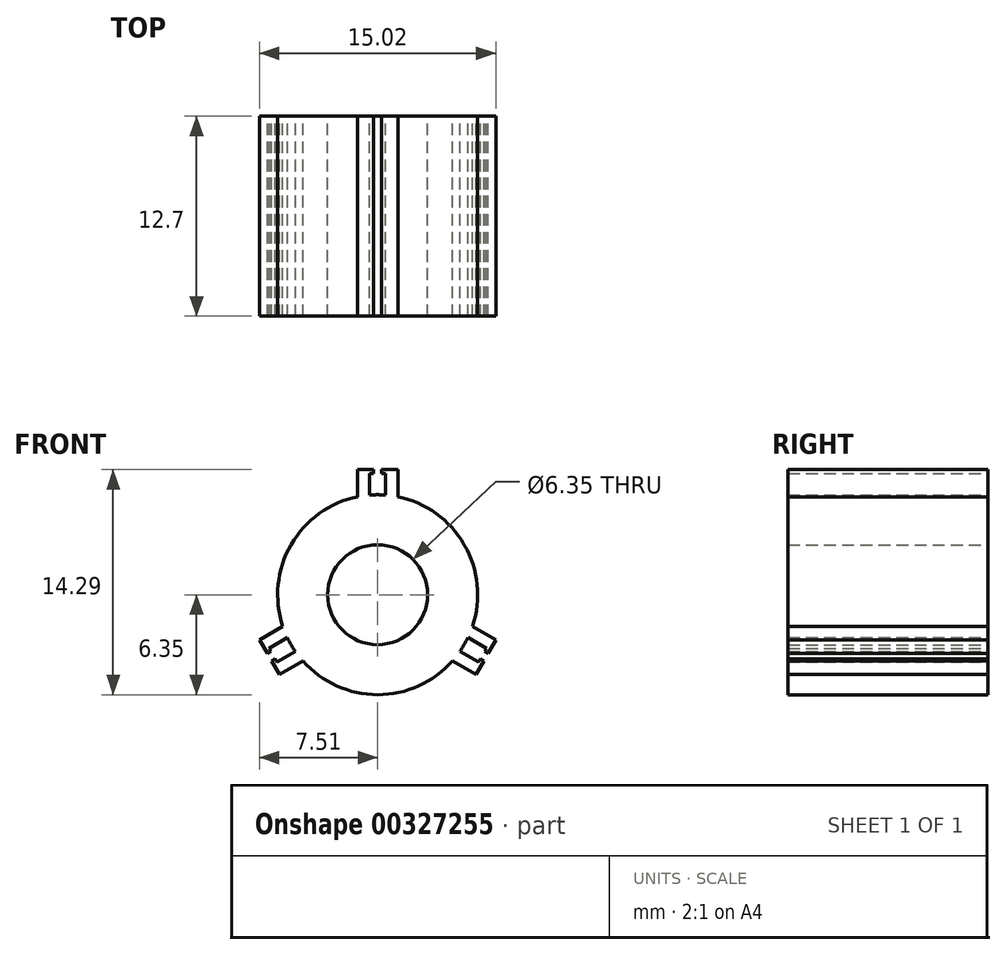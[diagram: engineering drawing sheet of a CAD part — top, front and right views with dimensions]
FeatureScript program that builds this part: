
annotation { "Feature Type Name" : "Feature", "Feature Type Description" : "" }
export const myFeature = defineFeature(function(context is Context, id is Id, definition is map)
    precondition{}
    {
        {
            var Q0;
            Q0=qCreatedBy(makeId("Front.planeOp"),FACE);
            var sketch = newSketch(context, id + "F0", { "sketchPlane" : qUnion([Q0])});
            skArc(sketch, "E0", {"start": v(0.5, 6.33) * mm, "mid": v(0, 6.35) * mm, "end": v(-0.5, 6.33) * mm});
            skLineSegment(sketch, "E1", {"start": v(0.5, 6.33) * mm, "end": v(0.5, 7.68) * mm});
            skLineSegment(sketch, "E2", {"start": v(0.5, 7.94) * mm, "end": v(1.28, 7.94) * mm});
            skLineSegment(sketch, "E3", {"start": v(1.28, 7.94) * mm, "end": v(1.28, 6.22) * mm});
            skLineSegment(sketch, "E4.MirrorCS", {"start": v(-1.28, 7.94) * mm, "end": v(-1.28, 6.22) * mm});
            skLineSegment(sketch, "E5.MirrorCS", {"start": v(-0.5, 6.33) * mm, "end": v(-0.5, 7.68) * mm});
            skLineSegment(sketch, "E6.MirrorCS", {"start": v(-0.5, 7.94) * mm, "end": v(-1.28, 7.94) * mm});
            skArc(sketch, "E7.trimOffspring", {"start": v(-1.28, 6.22) * mm, "mid": v(-5.5, 3.18) * mm, "end": v(-6.03, -2) * mm});
            skLineSegment(sketch, "E8.1.0", {"start": v(-5.23, -3.6) * mm, "end": v(-6.4, -4.28) * mm});
            skLineSegment(sketch, "E8.1.1", {"start": v(-6.24, -5.08) * mm, "end": v(-4.75, -4.22) * mm});
            skLineSegment(sketch, "E8.1.2", {"start": v(-6.62, -4.4) * mm, "end": v(-6.24, -5.08) * mm});
            skArc(sketch, "E8.1.3", {"start": v(-5.74, -2.73) * mm, "mid": v(-5.5, -3.17) * mm, "end": v(-5.23, -3.6) * mm});
            skLineSegment(sketch, "E8.1.4", {"start": v(-7.51, -2.86) * mm, "end": v(-6.03, -2) * mm});
            skLineSegment(sketch, "E8.1.5", {"start": v(-7.13, -3.53) * mm, "end": v(-7.51, -2.86) * mm});
            skLineSegment(sketch, "E8.1.6", {"start": v(-5.74, -2.73) * mm, "end": v(-6.9, -3.4) * mm});
            skLineSegment(sketch, "E8.2.0", {"start": v(5.74, -2.73) * mm, "end": v(6.9, -3.4) * mm});
            skLineSegment(sketch, "E8.2.1", {"start": v(7.51, -2.86) * mm, "end": v(6.03, -2) * mm});
            skLineSegment(sketch, "E8.2.2", {"start": v(7.13, -3.53) * mm, "end": v(7.51, -2.86) * mm});
            skArc(sketch, "E8.2.3", {"start": v(5.23, -3.6) * mm, "mid": v(5.5, -3.18) * mm, "end": v(5.74, -2.73) * mm});
            skLineSegment(sketch, "E8.2.4", {"start": v(6.24, -5.08) * mm, "end": v(4.75, -4.22) * mm});
            skLineSegment(sketch, "E8.2.5", {"start": v(6.62, -4.4) * mm, "end": v(6.24, -5.08) * mm});
            skLineSegment(sketch, "E8.2.6", {"start": v(5.23, -3.6) * mm, "end": v(6.4, -4.28) * mm});
            skArc(sketch, "E9.trimOffspring", {"start": v(-4.75, -4.22) * mm, "mid": v(0, -6.35) * mm, "end": v(4.75, -4.22) * mm});
            skArc(sketch, "E10.trimOffspring", {"start": v(6.03, -2) * mm, "mid": v(5.5, 3.17) * mm, "end": v(1.28, 6.22) * mm});
            skCircle(sketch, "E11", {"center": v(0, 0) * mm, "radius": 3.18 * mm});
            skLineSegment(sketch, "E12", {"start": v(-0.5, 7.94) * mm, "end": v(-0.26, 7.94) * mm});
            skLineSegment(sketch, "E13", {"start": v(-0.26, 7.94) * mm, "end": v(-0.26, 7.68) * mm});
            skLineSegment(sketch, "E14", {"start": v(-0.26, 7.68) * mm, "end": v(-0.5, 7.68) * mm});
            skLineSegment(sketch, "E15.MirrorCS", {"start": v(0.26, 7.68) * mm, "end": v(0.5, 7.68) * mm});
            skLineSegment(sketch, "E16.MirrorCS", {"start": v(0.26, 7.94) * mm, "end": v(0.26, 7.68) * mm});
            skLineSegment(sketch, "E17.MirrorCS", {"start": v(0.5, 7.94) * mm, "end": v(0.26, 7.94) * mm});
            skLineSegment(sketch, "E18.1.0", {"start": v(-6.75, -4.2) * mm, "end": v(-6.53, -4.07) * mm});
            skLineSegment(sketch, "E18.1.1", {"start": v(-6.62, -4.4) * mm, "end": v(-6.75, -4.2) * mm});
            skLineSegment(sketch, "E18.1.2", {"start": v(-6.53, -4.07) * mm, "end": v(-6.4, -4.28) * mm});
            skLineSegment(sketch, "E18.1.3", {"start": v(-7, -3.75) * mm, "end": v(-6.78, -3.62) * mm});
            skLineSegment(sketch, "E18.1.4", {"start": v(-7.13, -3.53) * mm, "end": v(-7, -3.75) * mm});
            skLineSegment(sketch, "E18.1.5", {"start": v(-6.78, -3.62) * mm, "end": v(-6.9, -3.4) * mm});
            skLineSegment(sketch, "E18.2.0", {"start": v(7, -3.75) * mm, "end": v(6.78, -3.62) * mm});
            skLineSegment(sketch, "E18.2.1", {"start": v(7.13, -3.53) * mm, "end": v(7, -3.75) * mm});
            skLineSegment(sketch, "E18.2.2", {"start": v(6.78, -3.62) * mm, "end": v(6.9, -3.4) * mm});
            skLineSegment(sketch, "E18.2.3", {"start": v(6.75, -4.2) * mm, "end": v(6.53, -4.07) * mm});
            skLineSegment(sketch, "E18.2.4", {"start": v(6.62, -4.4) * mm, "end": v(6.75, -4.2) * mm});
            skLineSegment(sketch, "E18.2.5", {"start": v(6.53, -4.07) * mm, "end": v(6.4, -4.28) * mm});
            skPoint(sketch, "E19.orphan", {"position": v(-6.62, -4.4) * mm});
            skPoint(sketch, "E20.orphan", {"position": v(7.13, -3.53) * mm});
            skSolve(sketch);
        }
        {
            var Q0;
            Q0=makeQuery(id+"F0.imprint","IMPRINT",FACE,{"disambiguationData":[TD([[makeQuery(id+"F0.imprint","IMPRINT",EDGE,{"derivedFrom":sQuery(id+"F0.wireOp",EDGE,"E0")}),1.0]])]});
            extrude(context, id + "F1", {"entities" : qUnion([Q0]), "depth" : 12.7 * mm});
        }
    });
